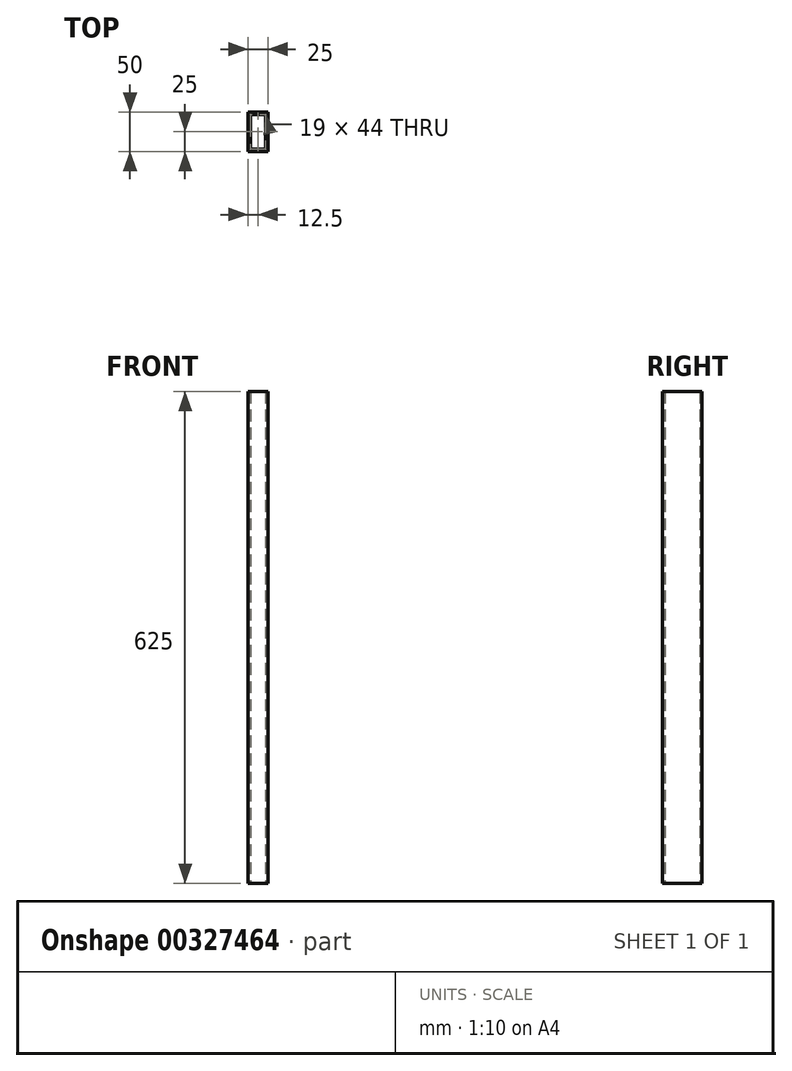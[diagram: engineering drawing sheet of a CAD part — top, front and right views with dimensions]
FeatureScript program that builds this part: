
annotation { "Feature Type Name" : "Feature", "Feature Type Description" : "" }
export const myFeature = defineFeature(function(context is Context, id is Id, definition is map)
    precondition{}
    {
        {
            var Q0;
            Q0=qCreatedBy(makeId("Top.planeOp"),FACE);
            var sketch = newSketch(context, id + "F0", { "sketchPlane" : qUnion([Q0])});
            skLineSegment(sketch, "E0.bottom", {"start": v(-12.5, -25) * mm, "end": v(12.5, -25) * mm});
            skLineSegment(sketch, "E0.top", {"start": v(-12.5, 25) * mm, "end": v(12.5, 25) * mm});
            skLineSegment(sketch, "E0.left", {"start": v(-12.5, -25) * mm, "end": v(-12.5, 25) * mm});
            skLineSegment(sketch, "E0.right", {"start": v(12.5, -25) * mm, "end": v(12.5, 25) * mm});
            skPoint(sketch, "E0.middle", {"position": v(0, 0) * mm});
            skLineSegment(sketch, "E1.bottom", {"start": v(-9.5, 22) * mm, "end": v(9.5, 22) * mm});
            skLineSegment(sketch, "E1.top", {"start": v(-9.5, -22) * mm, "end": v(9.5, -22) * mm});
            skLineSegment(sketch, "E1.left", {"start": v(-9.5, 22) * mm, "end": v(-9.5, -22) * mm});
            skLineSegment(sketch, "E1.right", {"start": v(9.5, 22) * mm, "end": v(9.5, -22) * mm});
            skSolve(sketch);
        }
        {
            var Q0;
            Q0=makeQuery(id+"F0.imprint","IMPRINT",FACE,{"disambiguationData":[TD([[makeQuery(id+"F0.imprint","IMPRINT",EDGE,{"derivedFrom":sQuery(id+"F0.wireOp",EDGE,"E0.bottom")}),1.0]])]});
            extrude(context, id + "F1", {"entities" : qUnion([Q0]), "depth" : 625 * mm, "symmetric" : true});
        }
    });
